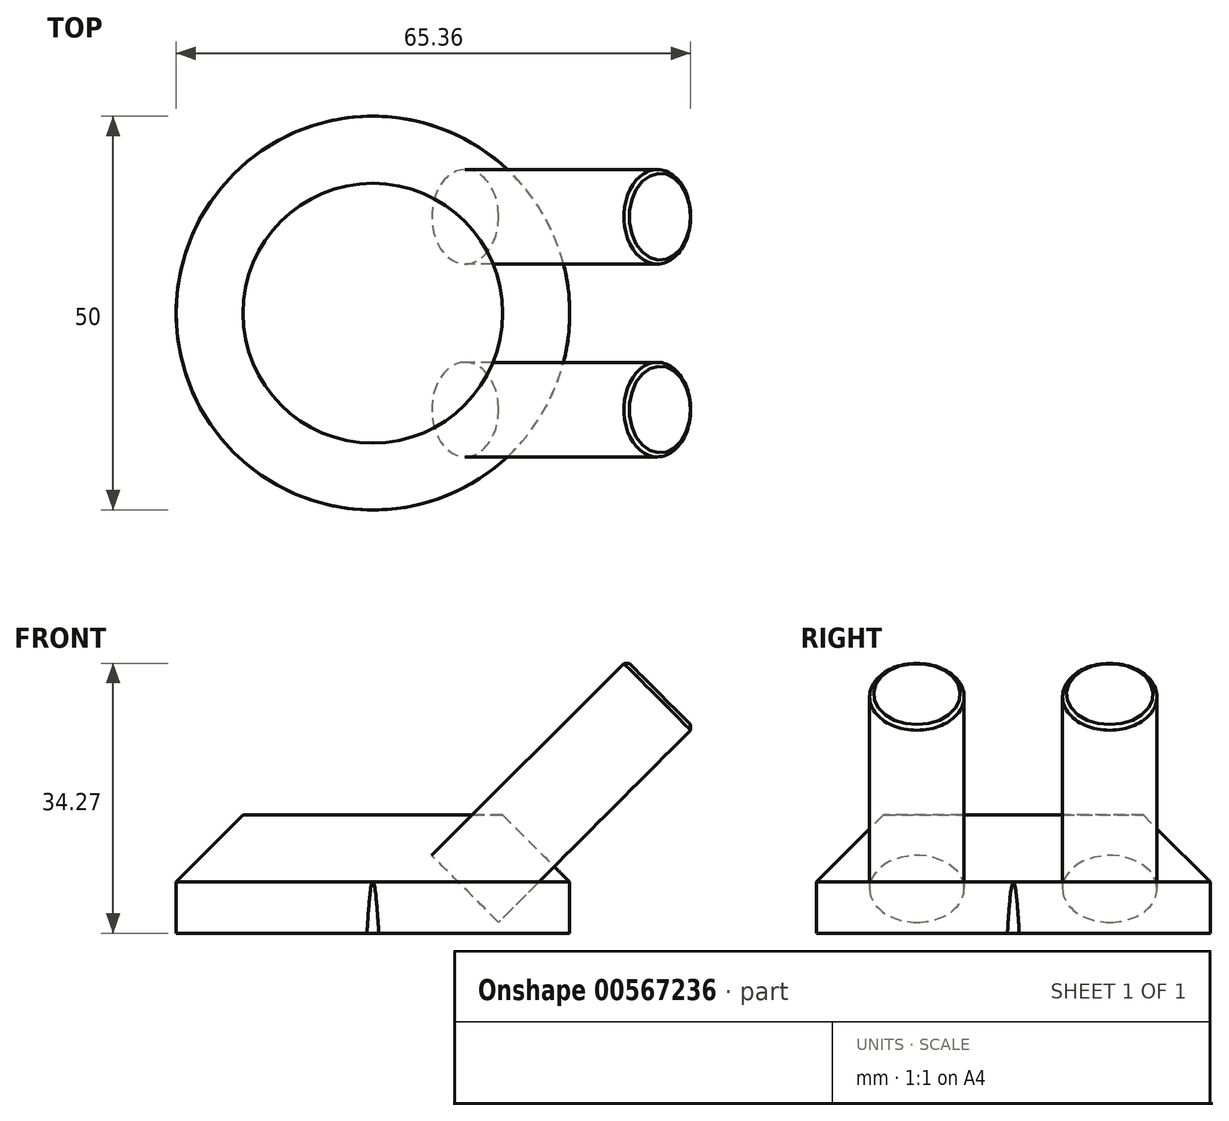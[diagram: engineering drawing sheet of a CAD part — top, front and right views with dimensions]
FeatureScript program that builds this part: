
annotation { "Feature Type Name" : "Feature", "Feature Type Description" : "" }
export const myFeature = defineFeature(function(context is Context, id is Id, definition is map)
    precondition{}
    {
        {
            var Q0;
            Q0=qCreatedBy(makeId("Top.planeOp"),FACE);
            var sketch = newSketch(context, id + "F0", { "sketchPlane" : qUnion([Q0])});
            skLineSegment(sketch, "E0.bottom", {"start": v(-25, 25) * mm, "end": v(25, 25) * mm});
            skLineSegment(sketch, "E0.top", {"start": v(-25, -25) * mm, "end": v(25, -25) * mm});
            skLineSegment(sketch, "E0.left", {"start": v(-25, 25) * mm, "end": v(-25, -25) * mm});
            skLineSegment(sketch, "E0.right", {"start": v(25, 25) * mm, "end": v(25, -25) * mm});
            skSolve(sketch);
        }
        {
            var Q0;
            Q0=qSketchRegion(id+"F0",true);
            extrude(context, id + "F1", {"entities" : qUnion([Q0]), "oppositeDirection" : true, "depth" : 15 * mm, "offsetDistance" : 25 * mm});
        }
        {
            var Q0;
            Q0=makeQuery(id+"F1.opExtrude","CAP_EDGE",EDGE,{"disambiguationData":[OSD([sQuery(id+"F0.wireOp",EDGE,"EIGbn9o8-BXwo-Xmxg-VTVW-IYnVgfDgFz95")])],"isStart":true});
            var Q1;
            Q1=makeQuery(id+"F1.opExtrude","CAP_EDGE",EDGE,{"disambiguationData":[OSD([sQuery(id+"F0.wireOp",EDGE,"E0.right")])],"isStart":true});
            chamfer(context, id + "F2", {"entities" : qUnion([Q0, Q1]), "width" : 8.5 * mm, "tangentPropagation" : true});
        }
        {
            var Q0;
            Q0=makeQuery(id+"F2.opChamfer","BLEND_FACE",FACE,{"disambiguationData":[OSD([sQuery(id+"F0.wireOp",EDGE,"E0.right")])]});
            var sketch = newSketch(context, id + "F3", { "sketchPlane" : qUnion([Q0])});
            skLineSegment(sketch, "E1", {"start": v(0, -11.67) * mm, "end": v(0, -23.69) * mm, "construction": true});
            skPoint(sketch, "E2.startSnap0", {"position": v(0, -17.68) * mm});
            skLineSegment(sketch, "E3", {"start": v(-12.25, -14.92) * mm, "end": v(12.25, -14.92) * mm, "construction": true});
            skCircle(sketch, "E4", {"center": v(-12.25, -14.92) * mm, "radius": 6 * mm});
            skCircle(sketch, "E5", {"center": v(12.25, -14.92) * mm, "radius": 6 * mm});
            skSolve(sketch);
        }
        {
            var Q0;
            Q0=qCreatedBy(makeId("Front.planeOp"),FACE);
            var sketch = newSketch(context, id + "F4", { "sketchPlane" : qUnion([Q0])});
            skPoint(sketch, "E6.0", {"position": v(16.5, 0) * mm});
            skPoint(sketch, "E7.0", {"position": v(25, -8.5) * mm});
            skLineSegment(sketch, "E8", {"start": v(25, -8.5) * mm, "end": v(16.5, 0) * mm});
            skLineSegment(sketch, "E9", {"start": v(0, 0) * mm, "end": v(0, -8.5) * mm});
            skLineSegment(sketch, "E10", {"start": v(57.64, 0) * mm, "end": v(16.5, 0) * mm});
            skLineSegment(sketch, "E11", {"start": v(57.64, 0) * mm, "end": v(57.64, -15) * mm});
            skLineSegment(sketch, "E12", {"start": v(57.64, -15) * mm, "end": v(25.01, -15) * mm});
            skLineSegment(sketch, "E13", {"start": v(25.01, -15) * mm, "end": v(25, -8.5) * mm});
            skSolve(sketch);
        }
        {
            var Q0;
            Q0=makeQuery(id+"F4.imprint","IMPRINT",FACE,{"disambiguationData":[TD([[makeQuery(id+"F4.imprint","IMPRINT",EDGE,{"derivedFrom":sQuery(id+"F4.wireOp",EDGE,"E8")}),-1.0]])]});
            var Q1;
            Q1=sQuery(id+"F4.wireOp",EDGE,"E9");
            revolve(context, id + "F5", {"operationType" : NewBodyOperationType.REMOVE, "entities" : qUnion([Q0]), "axis" : qUnion([Q1]), "revolveType" : RevolveType.ONE_DIRECTION, "angle" : 360 * degree});
        }
        {
            var Q0;
            Q0 = qSketchRegion(id + "F3", true);
            extrude(context, id + "F6", {"entities" : qUnion([Q0]), "depth" : 25 * mm, "offsetDistance" : 25 * mm, "hasSecondDirection" : true, "secondDirectionOppositeDirection" : true, "secondDirectionDepth" : 10 * mm});
        }
        {
            var Q0;
            Q0=makeQuery(id+"F6.opExtrude","CAP_EDGE",EDGE,{"disambiguationData":[OSD([sQuery(id+"F3.wireOp",EDGE,"E4")])],"isStart":false});
            var Q1;
            Q1=makeQuery(id+"F6.opExtrude","CAP_EDGE",EDGE,{"disambiguationData":[OSD([sQuery(id+"F3.wireOp",EDGE,"E5")])],"isStart":false});
            var Q2;
            Q2=makeQuery(id+"F5.boolean.opBoolean","COPY",EDGE,{"derivedFrom":makeQuery(id+"F5.opRevolve","SWEPT_EDGE",EDGE,{"disambiguationData":[OSD([sQuery(id+"F4.wireOp",EDGE,"E8"),sQuery(id+"F4.wireOp",EDGE,"E10")])]})});
            chamfer(context, id + "F7", {"entities" : qUnion([Q0, Q1, Q2]), "width" : .5 * mm, "tangentPropagation" : true});
        }
    });
